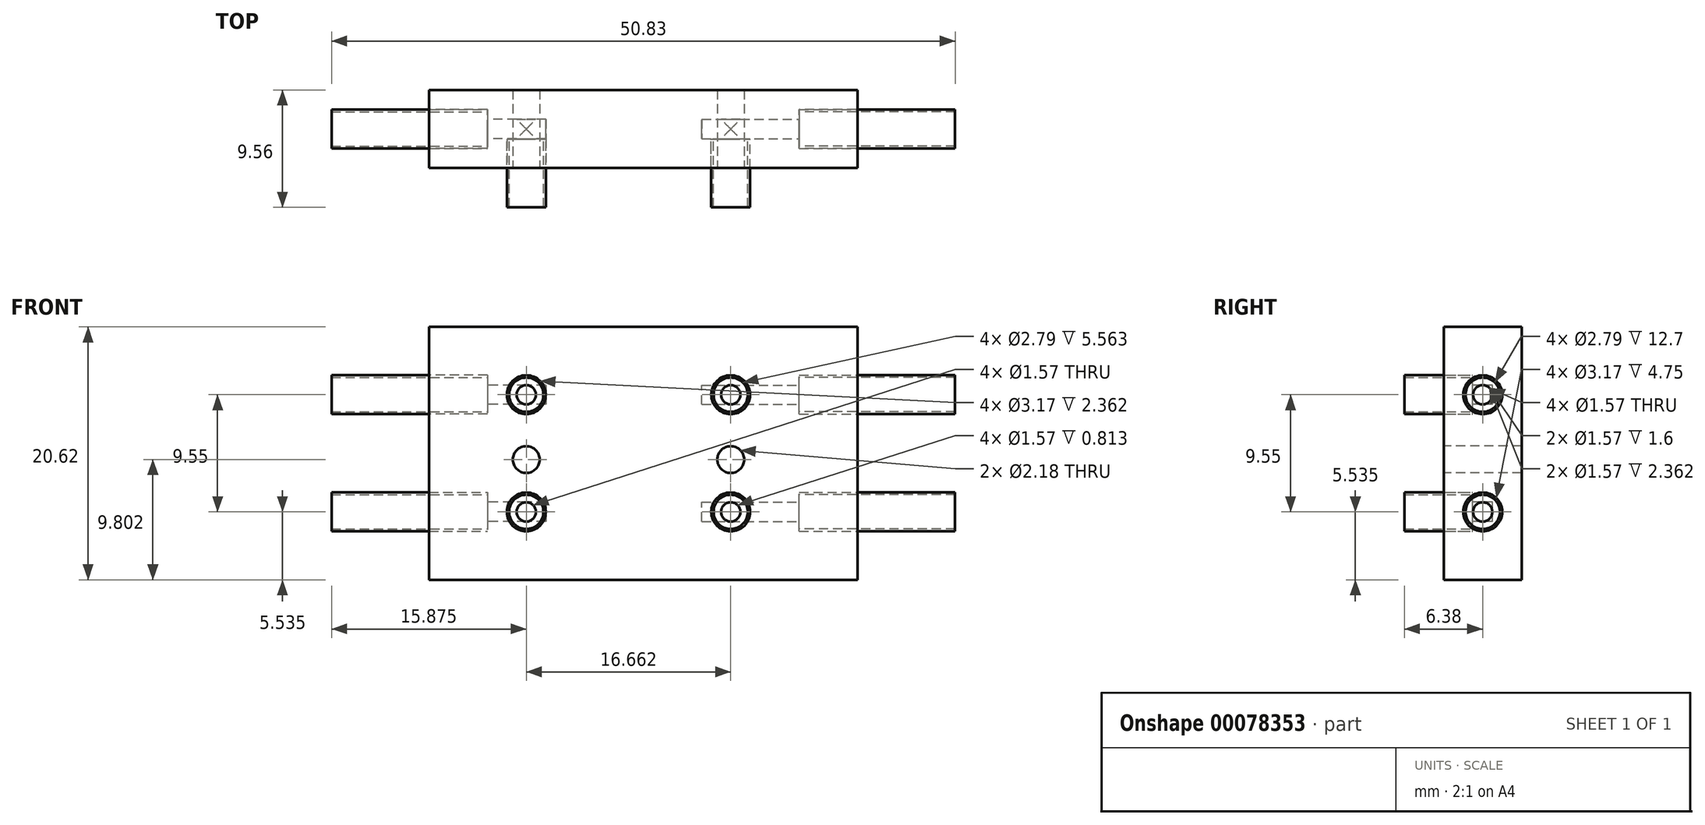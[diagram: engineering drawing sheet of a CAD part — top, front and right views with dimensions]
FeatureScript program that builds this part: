
annotation { "Feature Type Name" : "Feature", "Feature Type Description" : "" }
export const myFeature = defineFeature(function(context is Context, id is Id, definition is map)
    precondition{}
    {
        {
            var Q0;
            Q0=qCreatedBy(makeId("Front.planeOp"),FACE);
            var sketch = newSketch(context, id + "F0", { "sketchPlane" : qUnion([Q0])});
            skLineSegment(sketch, "E0.top", {"start": v(0, 10.31) * mm, "end": v(34.93, 10.31) * mm});
            skLineSegment(sketch, "E0.left", {"start": v(0, 0) * mm, "end": v(0, 10.31) * mm});
            skLineSegment(sketch, "E0.right", {"start": v(34.93, 0) * mm, "end": v(34.93, 10.31) * mm});
            skLineSegment(sketch, "E1.MirrorCS", {"start": v(34.93, 0) * mm, "end": v(34.93, -10.31) * mm});
            skLineSegment(sketch, "E2.MirrorCS", {"start": v(0, -10.31) * mm, "end": v(34.93, -10.31) * mm});
            skLineSegment(sketch, "E3.MirrorCS", {"start": v(0, 0) * mm, "end": v(0, -10.31) * mm});
            skSolve(sketch);
        }
        {
            var Q0;
            Q0 = qSketchRegion(id + "F0", true);
            extrude(context, id + "F1", {"entities" : qUnion([Q0]), "endBound" : BoundingType.SYMMETRIC, "depth" : 6.35 * mm});
        }
        {
            var Q0;
            Q0=makeQuery(id+"F1.opExtrude","CAP_FACE",FACE,{"disambiguationData":[OSD([sQuery(id+"F0.wireOp",EDGE,"E0.top"),sQuery(id+"F0.wireOp",EDGE,"E0.left"),sQuery(id+"F0.wireOp",EDGE,"E0.right"),sQuery(id+"F0.wireOp",EDGE,"E1.MirrorCS"),sQuery(id+"F0.wireOp",EDGE,"E2.MirrorCS"),sQuery(id+"F0.wireOp",EDGE,"E3.MirrorCS")])],"isStart":false});
            var sketch = newSketch(context, id + "F2", { "sketchPlane" : qUnion([Q0])});
            skLineSegment(sketch, "E4", {"start": v(0, 0) * mm, "end": v(7.92, 0) * mm, "construction": true});
            skLineSegment(sketch, "E5", {"start": v(0, 0) * mm, "end": v(0, 10.31) * mm});
            skLineSegment(sketch, "E6", {"start": v(0, 10.31) * mm, "end": v(7.92, 10.31) * mm});
            skLineSegment(sketch, "E7", {"start": v(7.92, 10.31) * mm, "end": v(7.92, -0.5) * mm, "construction": true});
            skLineSegment(sketch, "E8", {"start": v(0, -0.5) * mm, "end": v(24.59, -0.5) * mm, "construction": true});
            skCircle(sketch, "E9", {"center": v(7.92, -0.5) * mm, "radius": 1.1 * mm});
            skCircle(sketch, "E10", {"center": v(24.59, -0.5) * mm, "radius": 1.1 * mm});
            skSolve(sketch);
        }
        {
            var Q0;
            Q0 = qSketchRegion(id + "F2", true);
            extrude(context, id + "F3", {"entities" : qUnion([Q0]), "operationType" : NewBodyOperationType.REMOVE, "oppositeDirection" : true, "depth" : 50.8 * mm});
        }
        {
            var Q0;
            Q0=makeQuery(id+"F1.opExtrude","CAP_FACE",FACE,{"disambiguationData":[OSD([sQuery(id+"F0.wireOp",EDGE,"E0.top"),sQuery(id+"F0.wireOp",EDGE,"E0.left"),sQuery(id+"F0.wireOp",EDGE,"E0.right"),sQuery(id+"F0.wireOp",EDGE,"E1.MirrorCS"),sQuery(id+"F0.wireOp",EDGE,"E2.MirrorCS"),sQuery(id+"F0.wireOp",EDGE,"E3.MirrorCS")])],"isStart":false});
            var sketch = newSketch(context, id + "F4", { "sketchPlane" : qUnion([Q0])});
            skLineSegment(sketch, "E11", {"start": v(7.92, 10.31) * mm, "end": v(0, 10.31) * mm});
            skLineSegment(sketch, "E12", {"start": v(0, 10.31) * mm, "end": v(0, 0) * mm, "construction": true});
            skLineSegment(sketch, "E13", {"start": v(7.92, 10.31) * mm, "end": v(7.92, 4.78) * mm, "construction": true});
            skLineSegment(sketch, "E14", {"start": v(7.92, 10.31) * mm, "end": v(7.92, -4.78) * mm, "construction": true});
            skCircle(sketch, "E15", {"center": v(7.92, 4.78) * mm, "radius": 1.59 * mm});
            skCircle(sketch, "E16", {"center": v(7.92, -4.78) * mm, "radius": 1.59 * mm});
            skLineSegment(sketch, "E17", {"start": v(0, 10.31) * mm, "end": v(24.59, 10.31) * mm, "construction": true});
            skLineSegment(sketch, "E18", {"start": v(24.59, 10.31) * mm, "end": v(24.59, 4.78) * mm, "construction": true});
            skLineSegment(sketch, "E19", {"start": v(24.59, 4.78) * mm, "end": v(24.59, -4.78) * mm, "construction": true});
            skCircle(sketch, "E20", {"center": v(24.59, 4.78) * mm, "radius": 1.59 * mm});
            skCircle(sketch, "E21", {"center": v(24.59, -4.78) * mm, "radius": 1.59 * mm});
            skSolve(sketch);
        }
        {
            var Q0;
            Q0=makeQuery(id+"F4.imprint","IMPRINT",FACE,{"disambiguationData":[TD([[makeQuery(id+"F4.imprint","IMPRINT",EDGE,{"derivedFrom":sQuery(id+"F4.wireOp",EDGE,"E15")}),1.0]])]});
            var Q1;
            Q1=makeQuery(id+"F4.imprint","IMPRINT",FACE,{"disambiguationData":[TD([[makeQuery(id+"F4.imprint","IMPRINT",EDGE,{"derivedFrom":sQuery(id+"F4.wireOp",EDGE,"E16")}),1.0]])]});
            var Q2;
            Q2=makeQuery(id+"F4.imprint","IMPRINT",FACE,{"disambiguationData":[TD([[makeQuery(id+"F4.imprint","IMPRINT",EDGE,{"derivedFrom":sQuery(id+"F4.wireOp",EDGE,"E21")}),1.0]])]});
            var Q3;
            Q3=makeQuery(id+"F4.imprint","IMPRINT",FACE,{"disambiguationData":[TD([[makeQuery(id+"F4.imprint","IMPRINT",EDGE,{"derivedFrom":sQuery(id+"F4.wireOp",EDGE,"E20")}),1.0]])]});
            var Q4;
            Q4=sQuery(id+"F4.wireOp",EDGE,"E15");
            var Q5;
            Q5=sQuery(id+"F4.wireOp",EDGE,"E16");
            var Q6;
            Q6=sQuery(id+"F4.wireOp",EDGE,"E21");
            var Q7;
            Q7=sQuery(id+"F4.wireOp",EDGE,"E20");
            extrude(context, id + "F5", {"entities" : qUnion([Q0, Q1, Q2, Q3]), "operationType" : NewBodyOperationType.REMOVE, "surfaceEntities" : qUnion([Q4, Q5, Q6, Q7]), "oppositeDirection" : true, "depth" : 2.36 * mm});
        }
        {
            var Q0;
            Q0=makeQuery(id+"F1.opExtrude","CAP_FACE",FACE,{"disambiguationData":[OSD([sQuery(id+"F0.wireOp",EDGE,"E0.top"),sQuery(id+"F0.wireOp",EDGE,"E0.left"),sQuery(id+"F0.wireOp",EDGE,"E0.right"),sQuery(id+"F0.wireOp",EDGE,"E1.MirrorCS"),sQuery(id+"F0.wireOp",EDGE,"E2.MirrorCS"),sQuery(id+"F0.wireOp",EDGE,"E3.MirrorCS")])],"isStart":false});
            var sketch = newSketch(context, id + "F6", { "sketchPlane" : qUnion([Q0])});
            skCircle(sketch, "E22", {"center": v(7.92, 4.78) * mm, "radius": 0.79 * mm});
            skCircle(sketch, "E23", {"center": v(7.92, -4.78) * mm, "radius": 0.79 * mm});
            skCircle(sketch, "E24", {"center": v(24.59, -4.78) * mm, "radius": 0.79 * mm});
            skCircle(sketch, "E25", {"center": v(24.59, 4.78) * mm, "radius": 0.79 * mm});
            skSolve(sketch);
        }
        {
            var Q0;
            Q0 = qSketchRegion(id + "F6", true);
            extrude(context, id + "F7", {"entities" : qUnion([Q0]), "operationType" : NewBodyOperationType.REMOVE, "oppositeDirection" : true, "depth" : 4 * mm});
        }
        {
            var Q0;
            Q0=makeQuery(id+"F1.opExtrude","SWEPT_FACE",FACE,{"disambiguationData":[OSD([sQuery(id+"F0.wireOp",EDGE,"E0.left"),sQuery(id+"F0.wireOp",EDGE,"E3.MirrorCS")])]});
            var sketch = newSketch(context, id + "F8", { "sketchPlane" : qUnion([Q0])});
            skLineSegment(sketch, "E26", {"start": v(0, 0) * mm, "end": v(0, 10.31) * mm, "construction": true});
            skLineSegment(sketch, "E27", {"start": v(0, 10.31) * mm, "end": v(0, 4.78) * mm, "construction": true});
            skLineSegment(sketch, "E28", {"start": v(0, 10.31) * mm, "end": v(0, -4.78) * mm, "construction": true});
            skPoint(sketch, "E28.endSnap0", {"position": v(0, 7.54) * mm});
            skCircle(sketch, "E29", {"center": v(0, 4.78) * mm, "radius": 1.59 * mm});
            skCircle(sketch, "E30", {"center": v(0, -4.78) * mm, "radius": 1.59 * mm});
            skSolve(sketch);
        }
        {
            var Q0;
            Q0=makeQuery(id+"F8.imprint","IMPRINT",FACE,{"disambiguationData":[TD([[makeQuery(id+"F8.imprint","IMPRINT",EDGE,{"derivedFrom":sQuery(id+"F8.wireOp",EDGE,"E29")}),1.0]])]});
            var Q1;
            Q1=makeQuery(id+"F8.imprint","IMPRINT",FACE,{"disambiguationData":[TD([[makeQuery(id+"F8.imprint","IMPRINT",EDGE,{"derivedFrom":sQuery(id+"F8.wireOp",EDGE,"E30")}),1.0]])]});
            extrude(context, id + "F9", {"entities" : qUnion([Q0, Q1]), "operationType" : NewBodyOperationType.REMOVE, "oppositeDirection" : true, "depth" : 4.75 * mm});
        }
        {
            var Q0;
            Q0=makeQuery(id+"F1.opExtrude","SWEPT_FACE",FACE,{"disambiguationData":[OSD([sQuery(id+"F0.wireOp",EDGE,"E0.left"),sQuery(id+"F0.wireOp",EDGE,"E3.MirrorCS")])]});
            var sketch = newSketch(context, id + "F10", { "sketchPlane" : qUnion([Q0])});
            skCircle(sketch, "E31", {"center": v(0, 4.78) * mm, "radius": 0.79 * mm});
            skCircle(sketch, "E32", {"center": v(0, -4.78) * mm, "radius": 0.79 * mm});
            skSolve(sketch);
        }
        {
            var Q0;
            Q0 = qSketchRegion(id + "F10", true);
            extrude(context, id + "F11", {"entities" : qUnion([Q0]), "operationType" : NewBodyOperationType.REMOVE, "oppositeDirection" : true, "depth" : 9.52 * mm});
        }
        {
            var Q0;
            Q0=makeQuery(id+"F1.opExtrude","SWEPT_FACE",FACE,{"disambiguationData":[OSD([sQuery(id+"F0.wireOp",EDGE,"E0.right"),sQuery(id+"F0.wireOp",EDGE,"E1.MirrorCS")])]});
            var sketch = newSketch(context, id + "F12", { "sketchPlane" : qUnion([Q0])});
            skLineSegment(sketch, "E33", {"start": v(0, 0) * mm, "end": v(0, 10.31) * mm, "construction": true});
            skLineSegment(sketch, "E34", {"start": v(0, 10.31) * mm, "end": v(0, 4.78) * mm, "construction": true});
            skLineSegment(sketch, "E35", {"start": v(0, 10.31) * mm, "end": v(0, -4.78) * mm, "construction": true});
            skCircle(sketch, "E36", {"center": v(0, 4.78) * mm, "radius": 1.59 * mm});
            skCircle(sketch, "E37", {"center": v(0, -4.78) * mm, "radius": 1.59 * mm});
            skSolve(sketch);
        }
        {
            var Q0;
            Q0 = qSketchRegion(id + "F12", true);
            extrude(context, id + "F13", {"entities" : qUnion([Q0]), "operationType" : NewBodyOperationType.REMOVE, "oppositeDirection" : true, "depth" : 4.75 * mm});
        }
        {
            var Q0;
            Q0=makeQuery(id+"F1.opExtrude","SWEPT_FACE",FACE,{"disambiguationData":[OSD([sQuery(id+"F0.wireOp",EDGE,"E0.right"),sQuery(id+"F0.wireOp",EDGE,"E1.MirrorCS")])]});
            var sketch = newSketch(context, id + "F14", { "sketchPlane" : qUnion([Q0])});
            skCircle(sketch, "E38", {"center": v(0, 4.78) * mm, "radius": 0.79 * mm});
            skCircle(sketch, "E39", {"center": v(0, -4.78) * mm, "radius": 0.79 * mm});
            skSolve(sketch);
        }
        {
            var Q0;
            Q0 = qSketchRegion(id + "F14", true);
            extrude(context, id + "F15", {"entities" : qUnion([Q0]), "operationType" : NewBodyOperationType.REMOVE, "oppositeDirection" : true, "depth" : 12.7 * mm});
        }
        {
            var Q0;
            Q0=makeQuery(id+"F5.boolean.opBoolean","COPY",FACE,{"derivedFrom":makeQuery(id+"F5.opExtrude","CAP_FACE",FACE,{"disambiguationData":[OSD([sQuery(id+"F4.wireOp",EDGE,"E15")])],"isStart":false})});
            var sketch = newSketch(context, id + "F16", { "sketchPlane" : qUnion([Q0])});
            skCircle(sketch, "E40", {"center": v(7.92, 4.78) * mm, "radius": 1.59 * mm});
            skCircle(sketch, "E41", {"center": v(7.92, 4.78) * mm, "radius": 1.4 * mm});
            skSolve(sketch);
        }
        {
            var Q0;
            Q0=makeQuery(id+"F5.boolean.opBoolean","COPY",FACE,{"derivedFrom":makeQuery(id+"F5.opExtrude","CAP_FACE",FACE,{"disambiguationData":[OSD([sQuery(id+"F4.wireOp",EDGE,"E16")])],"isStart":false})});
            var sketch = newSketch(context, id + "F17", { "sketchPlane" : qUnion([Q0])});
            skCircle(sketch, "E42", {"center": v(7.92, -4.78) * mm, "radius": 1.59 * mm});
            skCircle(sketch, "E43", {"center": v(7.92, -4.78) * mm, "radius": 1.4 * mm});
            skSolve(sketch);
        }
        {
            var Q0;
            Q0=makeQuery(id+"F5.boolean.opBoolean","COPY",FACE,{"derivedFrom":makeQuery(id+"F5.opExtrude","CAP_FACE",FACE,{"disambiguationData":[OSD([sQuery(id+"F4.wireOp",EDGE,"E21")])],"isStart":false})});
            var sketch = newSketch(context, id + "F18", { "sketchPlane" : qUnion([Q0])});
            skCircle(sketch, "E44", {"center": v(24.59, -4.78) * mm, "radius": 1.59 * mm});
            skCircle(sketch, "E45", {"center": v(24.59, -4.78) * mm, "radius": 1.4 * mm});
            skSolve(sketch);
        }
        {
            var Q0;
            Q0=makeQuery(id+"F5.boolean.opBoolean","COPY",FACE,{"derivedFrom":makeQuery(id+"F5.opExtrude","CAP_FACE",FACE,{"disambiguationData":[OSD([sQuery(id+"F4.wireOp",EDGE,"E20")])],"isStart":false})});
            var sketch = newSketch(context, id + "F19", { "sketchPlane" : qUnion([Q0])});
            skCircle(sketch, "E46", {"center": v(24.59, 4.78) * mm, "radius": 1.59 * mm});
            skCircle(sketch, "E47", {"center": v(24.59, 4.78) * mm, "radius": 1.4 * mm});
            skSolve(sketch);
        }
        {
            var Q0;
            Q0 = qSketchRegion(id + "F19", true);
            var Q1;
            Q1 = qSketchRegion(id + "F18", true);
            var Q2;
            Q2 = qSketchRegion(id + "F17", true);
            var Q3;
            Q3 = qSketchRegion(id + "F16", true);
            extrude(context, id + "F20", {"entities" : qUnion([Q0, Q1, Q2, Q3]), "depth" : 5.56 * mm});
        }
        {
            var Q0;
            Q0=makeQuery(id+"F13.boolean.opBoolean","COPY",FACE,{"derivedFrom":makeQuery(id+"F13.opExtrude","CAP_FACE",FACE,{"disambiguationData":[OSD([sQuery(id+"F12.wireOp",EDGE,"E36")])],"isStart":false})});
            var sketch = newSketch(context, id + "F21", { "sketchPlane" : qUnion([Q0])});
            skCircle(sketch, "E48", {"center": v(0, 4.78) * mm, "radius": 1.59 * mm});
            skCircle(sketch, "E49", {"center": v(0, 4.78) * mm, "radius": 1.4 * mm});
            skSolve(sketch);
        }
        {
            var Q0;
            Q0=makeQuery(id+"F13.boolean.opBoolean","COPY",FACE,{"derivedFrom":makeQuery(id+"F13.opExtrude","CAP_FACE",FACE,{"disambiguationData":[OSD([sQuery(id+"F12.wireOp",EDGE,"E37")])],"isStart":false})});
            var sketch = newSketch(context, id + "F22", { "sketchPlane" : qUnion([Q0])});
            skCircle(sketch, "E50", {"center": v(0, -4.78) * mm, "radius": 1.59 * mm});
            skCircle(sketch, "E51", {"center": v(0, -4.78) * mm, "radius": 1.4 * mm});
            skSolve(sketch);
        }
        {
            var Q0;
            Q0 = qSketchRegion(id + "F22", true);
            var Q1;
            Q1 = qSketchRegion(id + "F21", true);
            extrude(context, id + "F23", {"entities" : qUnion([Q0, Q1]), "depth" : 12.7 * mm});
        }
        {
            var Q0;
            Q0=makeQuery(id+"F9.boolean.opBoolean","COPY",FACE,{"derivedFrom":makeQuery(id+"F9.opExtrude","CAP_FACE",FACE,{"disambiguationData":[OSD([sQuery(id+"F8.wireOp",EDGE,"E29")])],"isStart":false})});
            var sketch = newSketch(context, id + "F24", { "sketchPlane" : qUnion([Q0])});
            skCircle(sketch, "E52", {"center": v(0, 4.78) * mm, "radius": 1.59 * mm});
            skCircle(sketch, "E53", {"center": v(0, 4.78) * mm, "radius": 1.4 * mm});
            skSolve(sketch);
        }
        {
            var Q0;
            Q0=makeQuery(id+"F9.boolean.opBoolean","COPY",FACE,{"derivedFrom":makeQuery(id+"F9.opExtrude","CAP_FACE",FACE,{"disambiguationData":[OSD([sQuery(id+"F8.wireOp",EDGE,"E30")])],"isStart":false})});
            var sketch = newSketch(context, id + "F25", { "sketchPlane" : qUnion([Q0])});
            skCircle(sketch, "E54", {"center": v(0, -4.78) * mm, "radius": 1.59 * mm});
            skCircle(sketch, "E55", {"center": v(0, -4.78) * mm, "radius": 1.4 * mm});
            skSolve(sketch);
        }
        {
            var Q0;
            Q0 = qSketchRegion(id + "F25", true);
            var Q1;
            Q1 = qSketchRegion(id + "F24", true);
            extrude(context, id + "F26", {"entities" : qUnion([Q0, Q1]), "depth" : 12.7 * mm});
        }
    });
